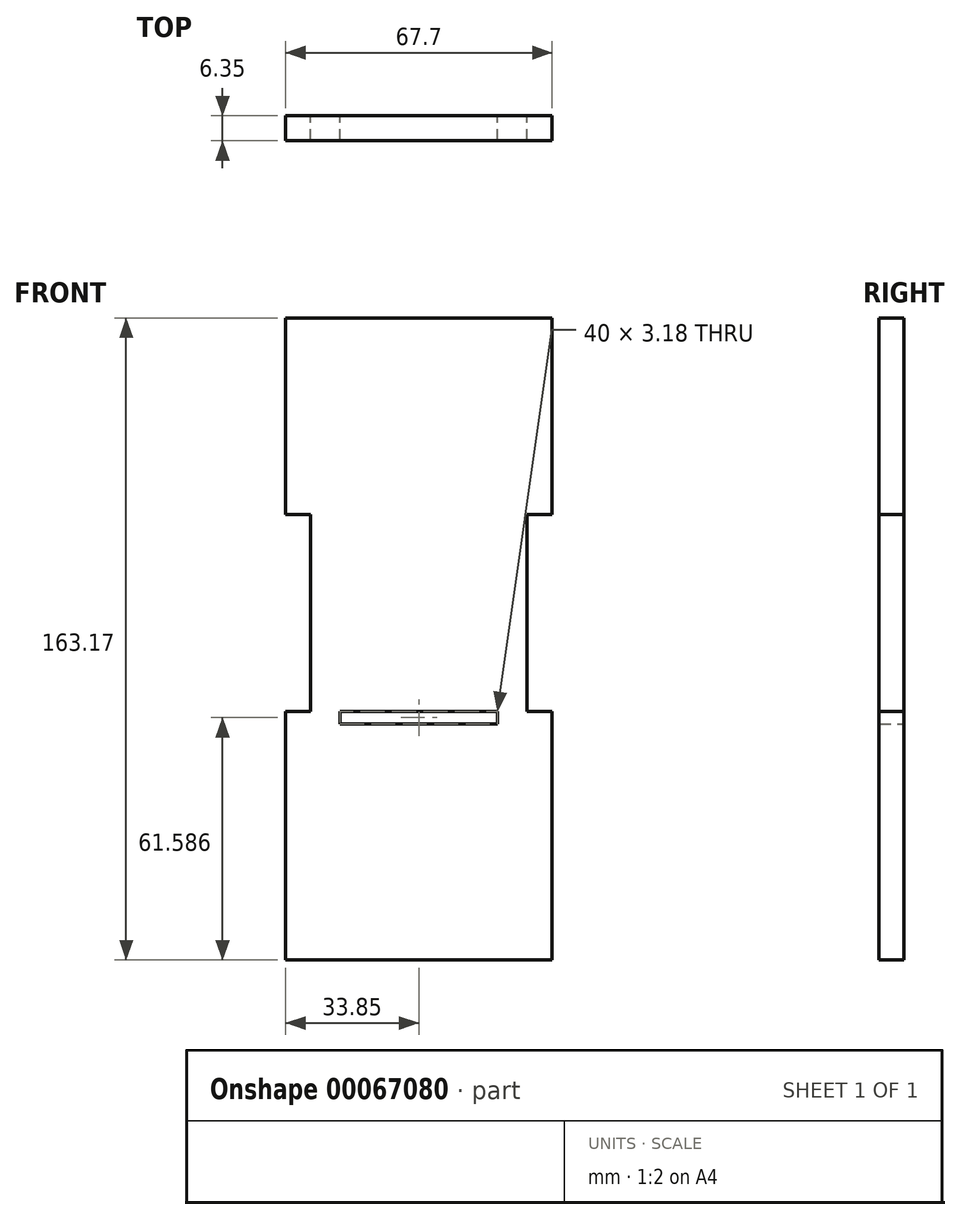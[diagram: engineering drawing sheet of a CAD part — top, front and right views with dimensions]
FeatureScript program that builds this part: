
annotation { "Feature Type Name" : "Feature", "Feature Type Description" : "" }
export const myFeature = defineFeature(function(context is Context, id is Id, definition is map)
    precondition{}
    {
        {
            var Q0;
            Q0=qCreatedBy(makeId("Front.planeOp"),FACE);
            var sketch = newSketch(context, id + "F0", { "sketchPlane" : qUnion([Q0])});
            skLineSegment(sketch, "E0.bottom", {"start": v(-33.85, 83.6) * mm, "end": v(33.85, 83.6) * mm});
            skLineSegment(sketch, "E0.top", {"start": v(-33.85, -79.58) * mm, "end": v(33.85, -79.58) * mm});
            skLineSegment(sketch, "E0.left", {"start": v(-33.85, 83.6) * mm, "end": v(-33.85, -79.58) * mm});
            skLineSegment(sketch, "E0.right", {"start": v(33.85, 83.6) * mm, "end": v(33.85, -79.58) * mm});
            skLineSegment(sketch, "E1.bottom", {"start": v(-20, -16.4) * mm, "end": v(20, -16.4) * mm});
            skLineSegment(sketch, "E1.top", {"start": v(-20, -19.58) * mm, "end": v(20, -19.58) * mm});
            skLineSegment(sketch, "E1.left", {"start": v(-20, -16.4) * mm, "end": v(-20, -19.58) * mm});
            skLineSegment(sketch, "E1.right", {"start": v(20, -16.4) * mm, "end": v(20, -19.58) * mm});
            skLineSegment(sketch, "E2.bottom", {"start": v(-33.85, 33.6) * mm, "end": v(-27.5, 33.6) * mm});
            skLineSegment(sketch, "E2.top", {"start": v(-33.85, -16.4) * mm, "end": v(-27.5, -16.4) * mm});
            skLineSegment(sketch, "E2.left", {"start": v(-33.85, 33.6) * mm, "end": v(-33.85, -16.4) * mm});
            skLineSegment(sketch, "E2.right", {"start": v(-27.5, 33.6) * mm, "end": v(-27.5, -16.4) * mm});
            skLineSegment(sketch, "E3.bottom", {"start": v(33.85, 33.6) * mm, "end": v(27.5, 33.6) * mm});
            skLineSegment(sketch, "E3.top", {"start": v(33.85, -16.4) * mm, "end": v(27.5, -16.4) * mm});
            skLineSegment(sketch, "E3.left", {"start": v(33.85, 33.6) * mm, "end": v(33.85, -16.4) * mm});
            skLineSegment(sketch, "E3.right", {"start": v(27.5, 33.6) * mm, "end": v(27.5, -16.4) * mm});
            skLineSegment(sketch, "E4", {"start": v(20, -19.58) * mm, "end": v(33.85, -19.58) * mm, "construction": true});
            skLineSegment(sketch, "E5", {"start": v(-20, -19.58) * mm, "end": v(-33.85, -19.58) * mm, "construction": true});
            skSolve(sketch);
        }
        {
            var Q0;
            {var subQ0=sQuery(id+"F0.wireOp",EDGE,"E0.bottom");Q0=makeQuery(id+"F0.imprint","IMPRINT",FACE,{"disambiguationData":[TD([[makeQuery(id+"F0.imprint","IMPRINT",EDGE,{"derivedFrom":subQ0}),-1.0]])]});}
            extrude(context, id + "F1", {"entities" : qUnion([Q0]), "depth" : 6.35 * mm});
        }
    });
